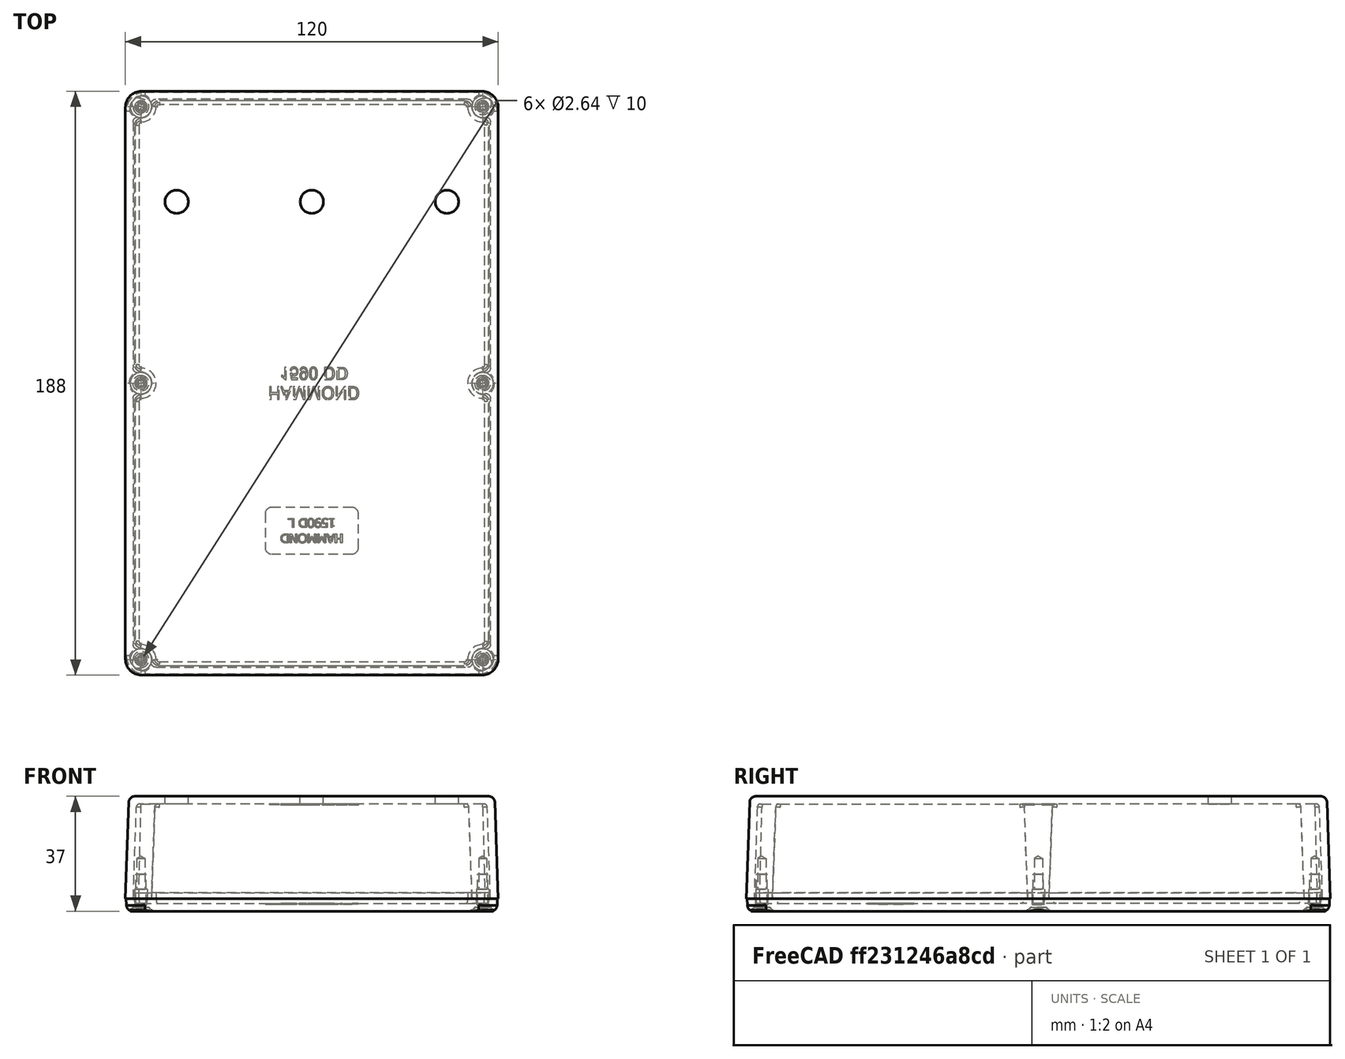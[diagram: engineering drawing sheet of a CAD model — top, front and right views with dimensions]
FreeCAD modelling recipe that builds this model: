
FCSTD DOCUMENT  (FreeCAD 0.19R18750 (Git))
Label: #700-000 With PCB
License: All rights reserved
LicenseURL: http://en.wikipedia.org/wiki/All_rights_reserved
objects: Part::Feature×8, Part::Cylinder×3, PartDesign::Plane×2, Part::MultiFuse×2, Part::Cut×1, PartDesign::ShapeBinder×1, PartDesign::Body×1, App::Link×1
note: 18 computed .brp shape members not serialized (recipe doc carries the construction recipe); baked Part::Feature solids carry a one-line shape summary decoded from their .brp
EXTERNAL_REF file=../#110-000 - Phasor PCB/#110-000 Assembly3.FCStd obj=LinkGroup

FEATURE [PartDesign::Plane] DatumPlane  label="DatumPlane_XY_Origin"
  AttachmentOffset = pos=(-100,-75,0) rot=(0,0,1;0rad)
  Length = 147.361
  MapMode = 5
  Placement = pos=(-100,-75,0) rot=(0,0,1;0rad)
  ResizeMode = 1
  Support = -> [XY_Plane001]
  Width = 150
FEATURE [Part::Feature] Part__Feature  label="#700-000 BOX"
  Placement = pos=(0,0,0) rot=(0.707107,-0.707107,0;3.14159rad)
  shape: bbox 120 x 188 x 451.1 mm, 273 faces (baked)
FEATURE [Part::Feature] Part__Feature001  label="1590D-DD-E LID"
  Placement = pos=(0,0,0) rot=(0,0.707107,0.707107;3.14159rad)
  shape: bbox 187.5 x 5.937 x 119.5 mm, 345 faces (baked)
FEATURE [Part::Feature] Part__Feature002  label="SC530 (screw #6-32X 1_2' FH)"
  Placement = pos=(1.2e-14,1.5362,-55) rot=(0,1,0;0.650238rad)
  shape: bbox 6.871 x 11.85 x 6.871 mm, 25 faces (baked)
FEATURE [Part::Feature] Part__Feature003  label="SC530 (screw #6-32X 1_2' FH)001"
  Placement = pos=(-1.2e-14,1.5362,55) rot=(0,1,0;0.650238rad)
  shape: bbox 6.871 x 11.85 x 6.871 mm, 25 faces (baked)
FEATURE [Part::Feature] Part__Feature004  label="SC530 (screw #6-32X 1_2' FH)002"
  Placement = pos=(-89,1.5362,55) rot=(0,1,0;0.650238rad)
  shape: bbox 6.871 x 11.85 x 6.871 mm, 25 faces (baked)
FEATURE [Part::Feature] Part__Feature005  label="SC530 (screw #6-32X 1_2' FH)003"
  Placement = pos=(-89,1.5362,-55) rot=(0,-1,0;0.529817rad)
  shape: bbox 6.871 x 11.85 x 6.871 mm, 25 faces (baked)
FEATURE [Part::Feature] Part__Feature006  label="SC530 (screw #6-32X 1_2' FH)004"
  Placement = pos=(89,1.5362,55) rot=(0,0,1;0rad)
  shape: bbox 6.871 x 11.85 x 6.871 mm, 25 faces (baked)
FEATURE [Part::Feature] Part__Feature007  label="SC530 (screw #6-32X 1_2' FH)005"
  Placement = pos=(89,1.5362,-55) rot=(0,0,1;0rad)
  shape: bbox 6.871 x 11.85 x 6.871 mm, 25 faces (baked)
FEATURE [Part::MultiFuse] Fusion  label="#700-000 LID & SCREWS"
  Placement = pos=(0,0,0) rot=(0.57735,-0.57735,0.57735;4.18879rad)
  Shapes = -> [Part__Feature001,Part__Feature004,Part__Feature003,Part__Feature005,Part__Feature002,Part__Feature006,Part__Feature007]
FEATURE [Part::Cylinder] Cylinder  label="CUTOUT POT RATE"
  Angle = 360
  AttacherType = Attacher::AttachEngine3D
  Height = 10
  Placement = pos=(-43.498,58.42,25) rot=(0,0,1;0rad)
  Radius = 3.75
FEATURE [Part::Cylinder] Cylinder001  label="CUTOUT POT DEPTH"
  Angle = 360
  AttacherType = Attacher::AttachEngine3D
  Height = 10
  Placement = pos=(0,58.42,25) rot=(0,0,1;0rad)
  Radius = 3.75
FEATURE [Part::Cylinder] Cylinder002  label="CUTOUT POT FEEDBACK"
  Angle = 360
  AttacherType = Attacher::AttachEngine3D
  Height = 10
  Placement = pos=(43.498,58.42,25) rot=(0,0,1;0rad)
  Radius = 3.75
FEATURE [Part::MultiFuse] Fusion001  label="CUTOUTS POTENTIOMETERS"
  Shapes = -> [Cylinder,Cylinder002,Cylinder001]
FEATURE [Part::Cut] Cut  label="#710-000 ENCLOSURE MACHINED"
  Base = -> Part__Feature
  Tool = -> Fusion001
FEATURE [PartDesign::ShapeBinder] CopyCut  label="ShapeBinder_Enclosure_Face"
  TraceSupport = false
FEATURE [PartDesign::Plane] DatumPlane001  label="DatumPlane_XY_Enclosure_Face"
  Length = 60
  MapMode = 5
  Placement = pos=(0,0,30.5) rot=(1,0,0;3.14159rad)
  ResizeMode = 0
  Support = -> [CopyCut]
  Width = 60
FEATURE [PartDesign::Body] Body  label="DATUM REFERENCES"
  Group = -> [DatumPlane,DatumPlane001,CopyCut]
  Origin = -> Origin001
FEATURE [App::Link] Link090  label="#110-001"
  LinkPlacement = pos=(0,0,19) rot=(0,0,1;0rad)
  LinkedObject = -> <external ../#110-000 - Phasor PCB/#110-000 Assembly3.FCStd>#LinkGroup
  Placement = pos=(0,0,19) rot=(0,0,1;0rad)
